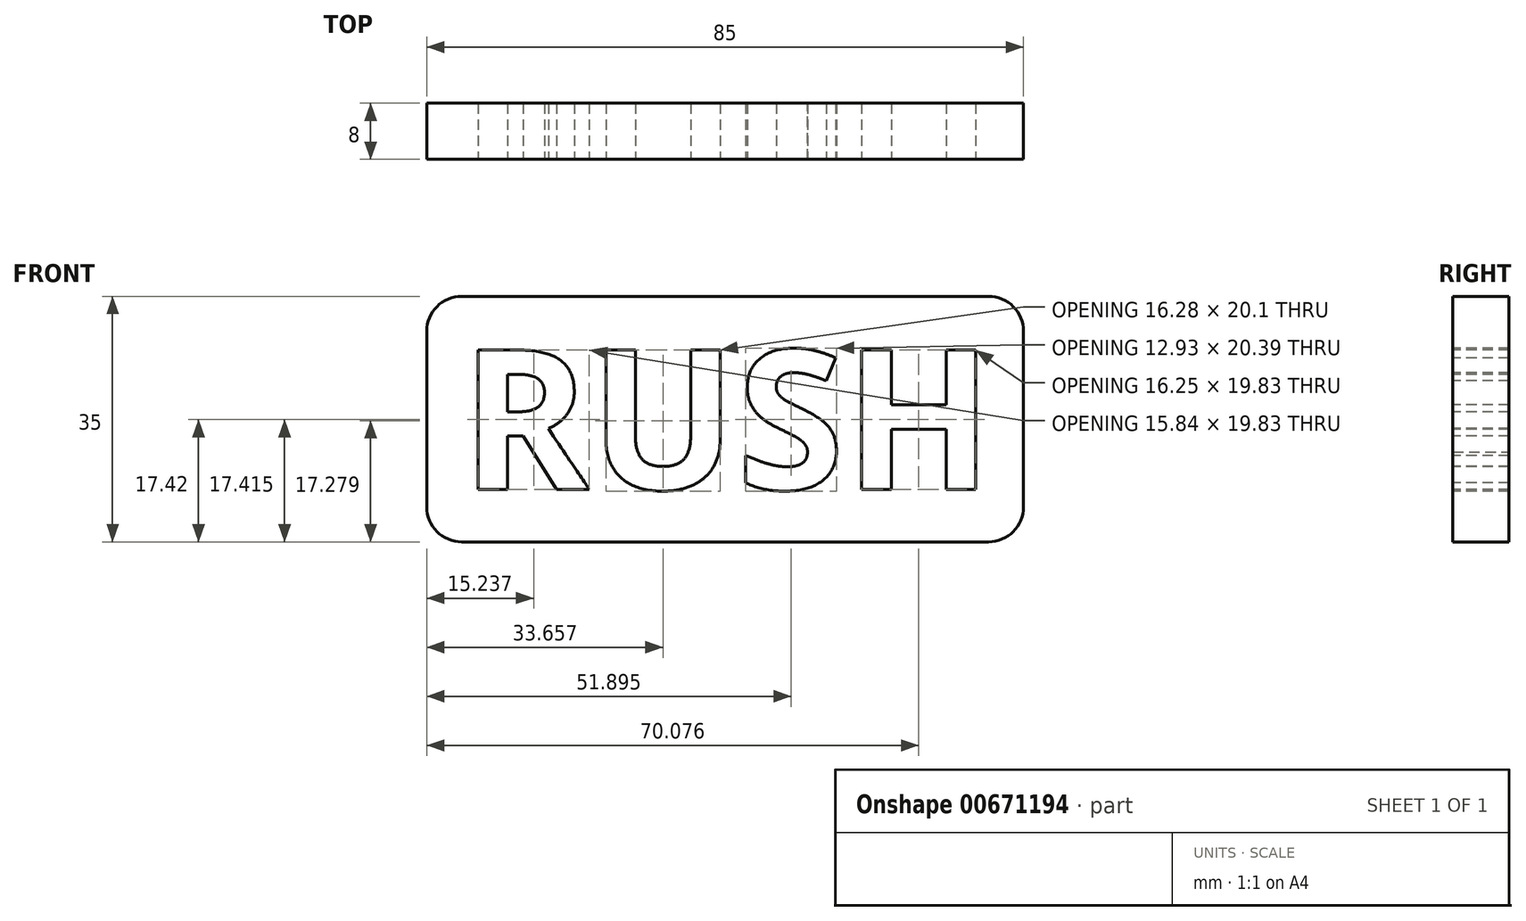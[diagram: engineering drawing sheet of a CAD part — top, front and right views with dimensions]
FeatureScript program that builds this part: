
annotation { "Feature Type Name" : "Feature", "Feature Type Description" : "" }
export const myFeature = defineFeature(function(context is Context, id is Id, definition is map)
    precondition{}
    {
        {
            var Q0;
            Q0=qCreatedBy(makeId("Front.planeOp"),FACE);
            var sketch = newSketch(context, id + "F0", { "sketchPlane" : qUnion([Q0])});
            skLineSegment(sketch, "E0.bottom", {"start": v(5, 0) * mm, "end": v(80, 0) * mm});
            skLineSegment(sketch, "E0.top", {"start": v(5, -35) * mm, "end": v(80, -35) * mm});
            skLineSegment(sketch, "E0.left", {"start": v(0, -5) * mm, "end": v(0, -30) * mm});
            skLineSegment(sketch, "E0.right", {"start": v(85, -5) * mm, "end": v(85, -30) * mm});
            skPoint(sketch, "E1.visualSharp", {"position": v(85, -35) * mm});
            skArc(sketch, "E1.filletArc", {"start": v(80, -35) * mm, "mid": v(83.54, -33.54) * mm, "end": v(85, -30) * mm});
            skPoint(sketch, "E2.visualSharp", {"position": v(0, -35) * mm});
            skArc(sketch, "E2.filletArc", {"start": v(0, -30) * mm, "mid": v(1.46, -33.54) * mm, "end": v(5, -35) * mm});
            skPoint(sketch, "E3.visualSharp", {"position": v(0, 0) * mm});
            skArc(sketch, "E3.filletArc", {"start": v(5, 0) * mm, "mid": v(1.46, -1.46) * mm, "end": v(0, -5) * mm});
            skPoint(sketch, "E4.visualSharp", {"position": v(85, 0) * mm});
            skArc(sketch, "E4.filletArc", {"start": v(85, -5) * mm, "mid": v(83.54, -1.46) * mm, "end": v(80, 0) * mm});
            skSolve(sketch);
        }
        {
            var Q0;
            Q0 = qSketchRegion(id + "F0", true);
            extrude(context, id + "F1", {"entities" : qUnion([Q0]), "depth" : 8 * mm, "offsetDistance" : 25 * mm});
        }
        {
            var Q0;
            Q0=makeQuery(id+"F1.opExtrude","CAP_FACE",FACE,{"disambiguationData":[OSD([sQuery(id+"F0.wireOp",EDGE,"E0.bottom"),sQuery(id+"F0.wireOp",EDGE,"E0.top"),sQuery(id+"F0.wireOp",EDGE,"E0.left"),sQuery(id+"F0.wireOp",EDGE,"E0.right"),sQuery(id+"F0.wireOp",EDGE,"E1.filletArc"),sQuery(id+"F0.wireOp",EDGE,"E2.filletArc"),sQuery(id+"F0.wireOp",EDGE,"E3.filletArc"),sQuery(id+"F0.wireOp",EDGE,"E4.filletArc")])],"isStart":false});
            var sketch = newSketch(context, id + "F2", { "sketchPlane" : qUnion([Q0])});
            skText(sketch, "E5", { "text": "RUSH", "fontName": "OpenSans-Bold.ttf"});
            const initialGuessF2  = {"E5": [0.00482, -0.0275, 1, 0, 0.02]};
            skSetInitialGuess(sketch, initialGuessF2);
            skSolve(sketch);
        }
        {
            var Q0;
            Q0 = qSketchRegion(id + "F2", true);
            extrude(context, id + "F3", {"entities" : qUnion([Q0]), "operationType" : NewBodyOperationType.REMOVE, "oppositeDirection" : true, "depth" : 25 * mm, "offsetDistance" : 25 * mm});
        }
    });
